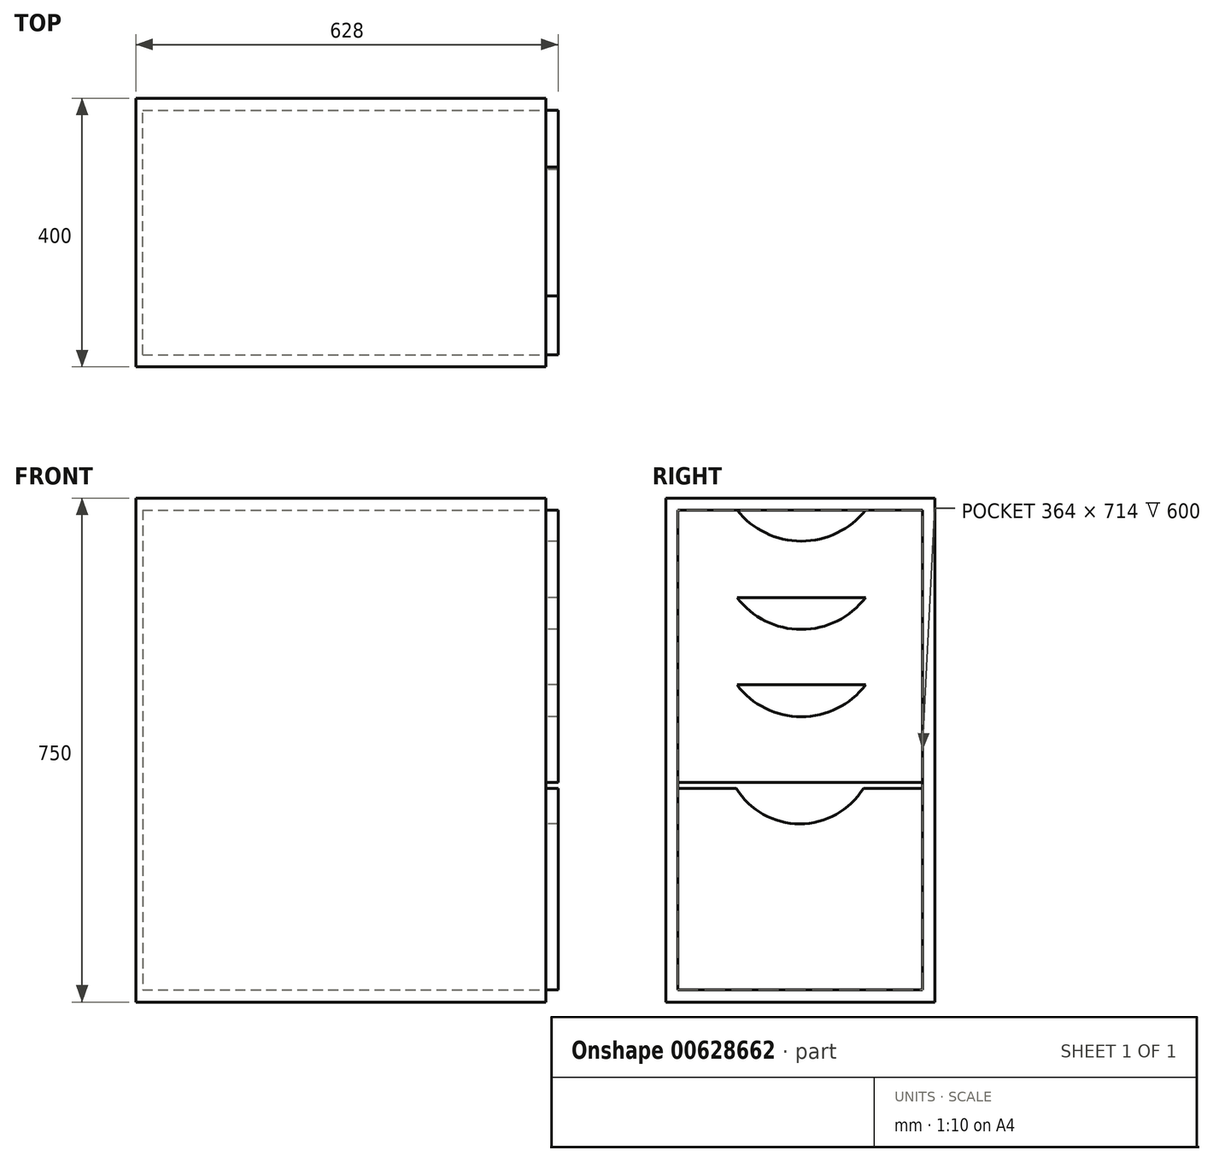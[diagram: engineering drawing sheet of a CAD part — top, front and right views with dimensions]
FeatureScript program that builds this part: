
annotation { "Feature Type Name" : "Feature", "Feature Type Description" : "" }
export const myFeature = defineFeature(function(context is Context, id is Id, definition is map)
    precondition{}
    {
        {
            var Q0;
            Q0=qCreatedBy(makeId("Right.planeOp"),FACE);
            var sketch = newSketch(context, id + "F0", { "sketchPlane" : qUnion([Q0])});
            skLineSegment(sketch, "E0.bottom", {"start": v(-200, 375) * mm, "end": v(200, 375) * mm});
            skLineSegment(sketch, "E0.top", {"start": v(-200, -375) * mm, "end": v(200, -375) * mm});
            skLineSegment(sketch, "E0.left", {"start": v(-200, 375) * mm, "end": v(-200, -375) * mm});
            skLineSegment(sketch, "E0.right", {"start": v(200, 375) * mm, "end": v(200, -375) * mm});
            skPoint(sketch, "E0.middle", {"position": v(0, 0) * mm});
            skLineSegment(sketch, "E1.bottom", {"start": v(-182, 357) * mm, "end": v(182, 357) * mm});
            skLineSegment(sketch, "E1.top", {"start": v(-182, -357) * mm, "end": v(182, -357) * mm});
            skLineSegment(sketch, "E1.left", {"start": v(-182, 357) * mm, "end": v(-182, -357) * mm});
            skLineSegment(sketch, "E1.right", {"start": v(182, 357) * mm, "end": v(182, -357) * mm});
            skSolve(sketch);
        }
        {
            var Q0;
            Q0=makeQuery(id+"F0.imprint","IMPRINT",FACE,{"disambiguationData":[TD([[makeQuery(id+"F0.imprint","IMPRINT",EDGE,{"derivedFrom":sQuery(id+"F0.wireOp",EDGE,"E0.bottom")}),-1.0]])]});
            extrude(context, id + "F1", {"entities" : qUnion([Q0]), "oppositeDirection" : true, "depth" : 600 * mm, "offsetDistance" : 25 * mm});
        }
        {
            var Q0;
            Q0=makeQuery(id+"F1.opExtrude","CAP_FACE",FACE,{"disambiguationData":[OSD([sQuery(id+"F0.wireOp",EDGE,"E0.bottom"),sQuery(id+"F0.wireOp",EDGE,"E0.top"),sQuery(id+"F0.wireOp",EDGE,"E0.left"),sQuery(id+"F0.wireOp",EDGE,"E0.right"),sQuery(id+"F0.wireOp",EDGE,"E1.bottom"),sQuery(id+"F0.wireOp",EDGE,"E1.top"),sQuery(id+"F0.wireOp",EDGE,"E1.left"),sQuery(id+"F0.wireOp",EDGE,"E1.right")])],"isStart":false});
            var sketch = newSketch(context, id + "F2", { "sketchPlane" : qUnion([Q0])});
            skLineSegment(sketch, "E2.bottom", {"start": v(-200, 375) * mm, "end": v(200, 375) * mm});
            skLineSegment(sketch, "E2.top", {"start": v(-200, -375) * mm, "end": v(200, -375) * mm});
            skLineSegment(sketch, "E2.left", {"start": v(-200, 375) * mm, "end": v(-200, -375) * mm});
            skLineSegment(sketch, "E2.right", {"start": v(200, 375) * mm, "end": v(200, -375) * mm});
            skPoint(sketch, "E2.middle", {"position": v(0, 0) * mm});
            skSolve(sketch);
        }
        {
            var Q0;
            Q0 = qSketchRegion(id + "F2", true);
            extrude(context, id + "F3", {"entities" : qUnion([Q0]), "operationType" : NewBodyOperationType.ADD, "depth" : 10 * mm, "offsetDistance" : 25 * mm});
        }
        {
            var Q0;
            Q0=makeQuery(id+"F1.opExtrude","CAP_FACE",FACE,{"disambiguationData":[OSD([sQuery(id+"F0.wireOp",EDGE,"E0.bottom"),sQuery(id+"F0.wireOp",EDGE,"E0.top"),sQuery(id+"F0.wireOp",EDGE,"E0.left"),sQuery(id+"F0.wireOp",EDGE,"E0.right"),sQuery(id+"F0.wireOp",EDGE,"E1.bottom"),sQuery(id+"F0.wireOp",EDGE,"E1.top"),sQuery(id+"F0.wireOp",EDGE,"E1.left"),sQuery(id+"F0.wireOp",EDGE,"E1.right")])],"isStart":true});
            var sketch = newSketch(context, id + "F4", { "sketchPlane" : qUnion([Q0])});
            skLineSegment(sketch, "E3.bottom", {"start": v(-182, -357) * mm, "end": v(182, -357) * mm});
            skLineSegment(sketch, "E3.top", {"start": v(-182, -57) * mm, "end": v(182, -57) * mm});
            skLineSegment(sketch, "E3.left", {"start": v(-182, -357) * mm, "end": v(-182, -57) * mm});
            skLineSegment(sketch, "E3.right", {"start": v(182, -357) * mm, "end": v(182, -57) * mm});
            skArc(sketch, "E4", {"start": v(-95.12, -57) * mm, "mid": v(-0.62, -109.82) * mm, "end": v(93.89, -57) * mm});
            skSolve(sketch);
        }
        {
            var Q0;
            Q0=makeQuery(id+"F1.opExtrude","CAP_FACE",FACE,{"disambiguationData":[OSD([sQuery(id+"F0.wireOp",EDGE,"E0.bottom"),sQuery(id+"F0.wireOp",EDGE,"E0.top"),sQuery(id+"F0.wireOp",EDGE,"E0.left"),sQuery(id+"F0.wireOp",EDGE,"E0.right"),sQuery(id+"F0.wireOp",EDGE,"E1.bottom"),sQuery(id+"F0.wireOp",EDGE,"E1.top"),sQuery(id+"F0.wireOp",EDGE,"E1.left"),sQuery(id+"F0.wireOp",EDGE,"E1.right")])],"isStart":true});
            var sketch = newSketch(context, id + "F5", { "sketchPlane" : qUnion([Q0])});
            skLineSegment(sketch, "E5.bottom", {"start": v(-182, 357) * mm, "end": v(182, 357) * mm});
            skLineSegment(sketch, "E5.top", {"start": v(-182, 227) * mm, "end": v(182, 227) * mm});
            skLineSegment(sketch, "E5.left", {"start": v(-182, 357) * mm, "end": v(-182, 227) * mm});
            skLineSegment(sketch, "E5.right", {"start": v(182, 357) * mm, "end": v(182, 227) * mm});
            skLineSegment(sketch, "E6.top", {"start": v(-182, 97) * mm, "end": v(182, 97) * mm});
            skLineSegment(sketch, "E6.left", {"start": v(-182, 227) * mm, "end": v(-182, 97) * mm});
            skLineSegment(sketch, "E6.right", {"start": v(182, 227) * mm, "end": v(182, 97) * mm});
            skArc(sketch, "E7", {"start": v(-94.04, 357) * mm, "mid": v(1.6, 310.8) * mm, "end": v(97.22, 357) * mm});
            skArc(sketch, "E8", {"start": v(-94.04, 227) * mm, "mid": v(1.6, 179.49) * mm, "end": v(97.22, 227) * mm});
            skLineSegment(sketch, "E9.top", {"start": v(-182, -48) * mm, "end": v(182, -48) * mm});
            skLineSegment(sketch, "E9.left", {"start": v(-182, 97) * mm, "end": v(-182, -48) * mm});
            skLineSegment(sketch, "E9.right", {"start": v(182, 97) * mm, "end": v(182, -48) * mm});
            skArc(sketch, "E10", {"start": v(-94.04, 97) * mm, "mid": v(1.6, 49.49) * mm, "end": v(97.22, 97) * mm});
            skSolve(sketch);
        }
        {
            var Q0;
            Q0=makeQuery(id+"F5.imprint","IMPRINT",FACE,{"disambiguationData":[TD([[makeQuery(id+"F5.imprint","IMPRINT",EDGE,{"derivedFrom":sQuery(id+"F5.wireOp",EDGE,"E9.top")}),1.0]])]});
            extrude(context, id + "F6", {"entities" : qUnion([Q0]), "depth" : 18 * mm, "offsetDistance" : 25 * mm});
        }
        {
            var Q0;
            {var subQ1=sQuery(id+"F5.wireOp",EDGE,"E6.left");Q0=makeQuery(id+"F5.imprint","IMPRINT",FACE,{"disambiguationData":[TD([[makeQuery(id+"F5.imprint","IMPRINT",EDGE,{"derivedFrom":subQ1}),1.0]])]});}
            extrude(context, id + "F7", {"entities" : qUnion([Q0]), "operationType" : NewBodyOperationType.ADD, "depth" : 18 * mm, "offsetDistance" : 25 * mm});
        }
        {
            var Q0;
            {var subQ1=sQuery(id+"F5.wireOp",EDGE,"E5.left");Q0=makeQuery(id+"F5.imprint","IMPRINT",FACE,{"disambiguationData":[TD([[makeQuery(id+"F5.imprint","IMPRINT",EDGE,{"derivedFrom":subQ1}),1.0]])]});}
            extrude(context, id + "F8", {"entities" : qUnion([Q0]), "operationType" : NewBodyOperationType.ADD, "depth" : 18 * mm, "offsetDistance" : 25 * mm});
        }
        {
            var Q0;
            Q0=makeQuery(id+"F4.imprint","IMPRINT",FACE,{"disambiguationData":[TD([[makeQuery(id+"F4.imprint","IMPRINT",EDGE,{"derivedFrom":sQuery(id+"F4.wireOp",EDGE,"E3.bottom")}),1.0]])]});
            extrude(context, id + "F9", {"entities" : qUnion([Q0]), "depth" : 18 * mm, "offsetDistance" : 25 * mm});
        }
    });
